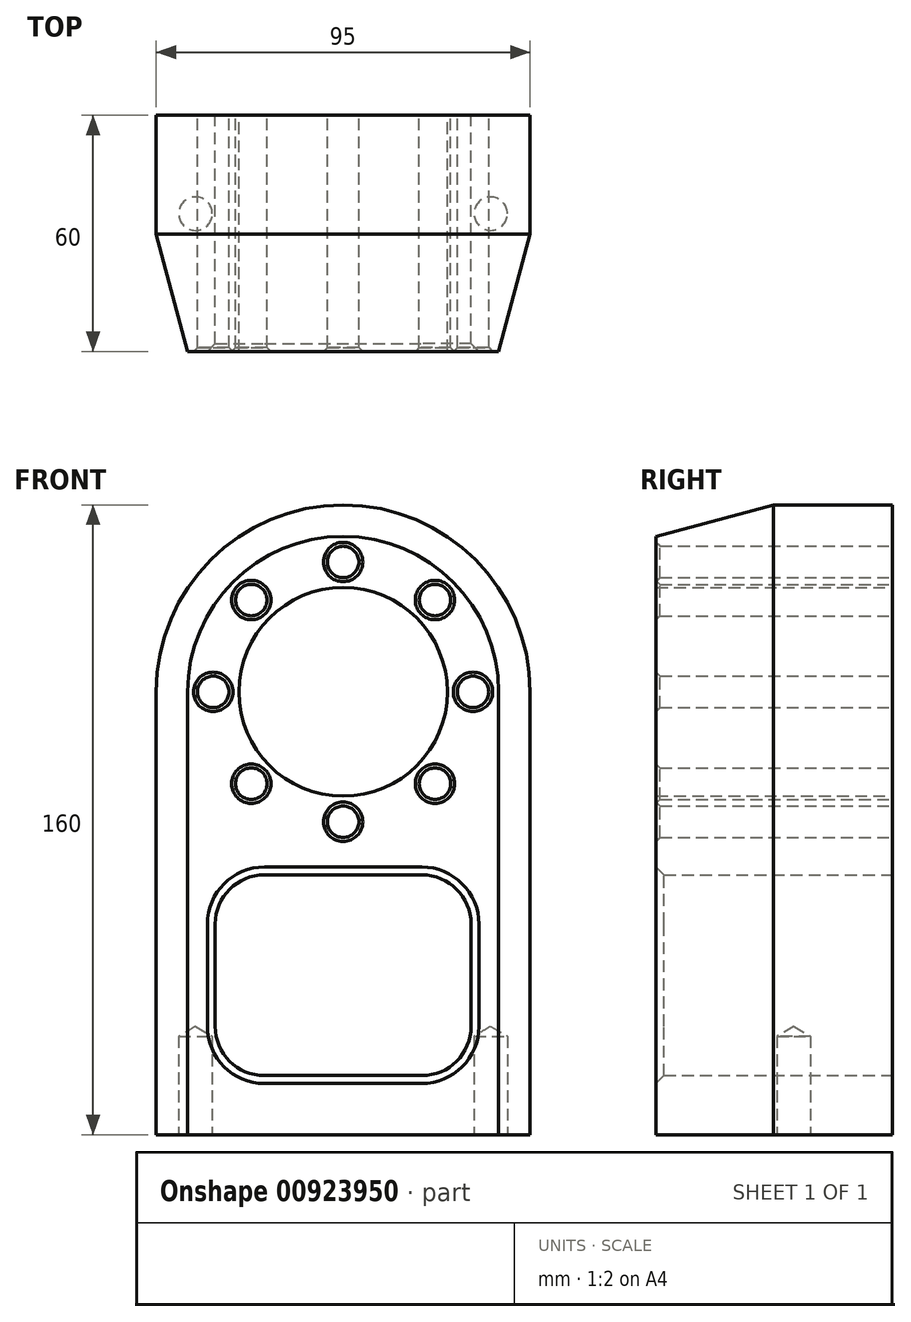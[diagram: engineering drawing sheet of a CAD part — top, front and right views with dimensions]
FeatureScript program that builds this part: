
annotation { "Feature Type Name" : "Feature", "Feature Type Description" : "" }
export const myFeature = defineFeature(function(context is Context, id is Id, definition is map)
    precondition{}
    {
        {
            var Q0;
            Q0=qCreatedBy(makeId("Front.planeOp"),FACE);
            var sketch = newSketch(context, id + "F0", { "sketchPlane" : qUnion([Q0])});
            skLineSegment(sketch, "E0.top", {"start": v(-46, -58.24) * mm, "end": v(49, -58.24) * mm});
            skLineSegment(sketch, "E0.left", {"start": v(-46, 54.26) * mm, "end": v(-46, -58.24) * mm});
            skLineSegment(sketch, "E0.right", {"start": v(49, 54.26) * mm, "end": v(49, -58.24) * mm});
            skArc(sketch, "E1", {"start": v(49, 54.26) * mm, "mid": v(1.5, 101.76) * mm, "end": v(-46, 54.26) * mm});
            skCircle(sketch, "E2", {"center": v(1.5, 54.26) * mm, "radius": 26.5 * mm});
            skLineSegment(sketch, "E3.bottom", {"start": v(-18.5, 7.76) * mm, "end": v(21.5, 7.76) * mm});
            skLineSegment(sketch, "E3.top", {"start": v(-18.5, -43.24) * mm, "end": v(21.5, -43.24) * mm});
            skLineSegment(sketch, "E3.left", {"start": v(-31, -4.74) * mm, "end": v(-31, -30.74) * mm});
            skLineSegment(sketch, "E3.right", {"start": v(34, -4.74) * mm, "end": v(34, -30.74) * mm});
            skPoint(sketch, "E4.visualSharp", {"position": v(-31, 7.76) * mm});
            skArc(sketch, "E4.filletArc", {"start": v(-18.5, 7.76) * mm, "mid": v(-27.34, 4.1) * mm, "end": v(-31, -4.74) * mm});
            skPoint(sketch, "E5.visualSharp", {"position": v(34, 7.76) * mm});
            skArc(sketch, "E5.filletArc", {"start": v(34, -4.74) * mm, "mid": v(30.34, 4.1) * mm, "end": v(21.5, 7.76) * mm});
            skPoint(sketch, "E6.visualSharp", {"position": v(34, -43.24) * mm});
            skArc(sketch, "E6.filletArc", {"start": v(21.5, -43.24) * mm, "mid": v(30.34, -39.58) * mm, "end": v(34, -30.74) * mm});
            skPoint(sketch, "E7.visualSharp", {"position": v(-31, -43.24) * mm});
            skArc(sketch, "E7.filletArc", {"start": v(-31, -30.74) * mm, "mid": v(-27.34, -39.58) * mm, "end": v(-18.5, -43.24) * mm});
            skLineSegment(sketch, "E8", {"start": v(1.5, 54.26) * mm, "end": v(-66.33, 54.26) * mm, "construction": true});
            skCircle(sketch, "E9", {"center": v(-31.5, 54.26) * mm, "radius": 4 * mm});
            skCircle(sketch, "E10.1.0", {"center": v(-21.83, 77.6) * mm, "radius": 4 * mm});
            skCircle(sketch, "E10.2.0", {"center": v(1.5, 87.26) * mm, "radius": 4 * mm});
            skCircle(sketch, "E10.3.0", {"center": v(24.84, 77.6) * mm, "radius": 4 * mm});
            skCircle(sketch, "E10.4.0", {"center": v(34.5, 54.26) * mm, "radius": 4 * mm});
            skCircle(sketch, "E10.5.0", {"center": v(24.84, 30.93) * mm, "radius": 4 * mm});
            skCircle(sketch, "E10.6.0", {"center": v(1.5, 21.26) * mm, "radius": 4 * mm});
            skCircle(sketch, "E10.7.0", {"center": v(-21.83, 30.93) * mm, "radius": 4 * mm});
            skSolve(sketch);
        }
        {
            var Q0;
            Q0 = qSketchRegion(id + "F0", true);
            extrude(context, id + "F1", {"entities" : qUnion([Q0]), "depth" : 60 * mm, "offsetDistance" : 25 * mm});
        }
        {
            var Q0;
            Q0=makeQuery(id+"F1.opExtrude","CAP_EDGE",EDGE,{"disambiguationData":[OSD([sQuery(id+"F0.wireOp",EDGE,"E9")])],"isStart":false});
            var Q1;
            Q1=makeQuery(id+"F1.opExtrude","CAP_EDGE",EDGE,{"disambiguationData":[OSD([sQuery(id+"F0.wireOp",EDGE,"E10.1.0")])],"isStart":false});
            var Q2;
            Q2=makeQuery(id+"F1.opExtrude","CAP_EDGE",EDGE,{"disambiguationData":[OSD([sQuery(id+"F0.wireOp",EDGE,"E10.2.0")])],"isStart":false});
            var Q3;
            Q3=makeQuery(id+"F1.opExtrude","CAP_EDGE",EDGE,{"disambiguationData":[OSD([sQuery(id+"F0.wireOp",EDGE,"E10.3.0")])],"isStart":false});
            var Q4;
            Q4=makeQuery(id+"F1.opExtrude","CAP_EDGE",EDGE,{"disambiguationData":[OSD([sQuery(id+"F0.wireOp",EDGE,"E10.4.0")])],"isStart":false});
            var Q5;
            Q5=makeQuery(id+"F1.opExtrude","CAP_EDGE",EDGE,{"disambiguationData":[OSD([sQuery(id+"F0.wireOp",EDGE,"E10.5.0")])],"isStart":false});
            var Q6;
            Q6=makeQuery(id+"F1.opExtrude","CAP_EDGE",EDGE,{"disambiguationData":[OSD([sQuery(id+"F0.wireOp",EDGE,"E10.6.0")])],"isStart":false});
            var Q7;
            Q7=makeQuery(id+"F1.opExtrude","CAP_EDGE",EDGE,{"disambiguationData":[OSD([sQuery(id+"F0.wireOp",EDGE,"E10.7.0")])],"isStart":false});
            chamfer(context, id + "F2", {"entities" : qUnion([Q0, Q1, Q2, Q3, Q4, Q5, Q6, Q7]), "width" : 1 * mm, "tangentPropagation" : true});
        }
        {
            var Q0;
            Q0=makeQuery(id+"F1.opExtrude","CAP_EDGE",EDGE,{"disambiguationData":[OSD([sQuery(id+"F0.wireOp",EDGE,"E3.bottom")])],"isStart":false});
            chamfer(context, id + "F3", {"entities" : qUnion([Q0]), "width" : 2 * mm, "tangentPropagation" : true});
        }
        {
            var Q0;
            Q0=makeQuery(id+"F1.opExtrude","CAP_EDGE",EDGE,{"disambiguationData":[OSD([sQuery(id+"F0.wireOp",EDGE,"E1")])],"isStart":false});
            chamfer(context, id + "F4", {"entities" : qUnion([Q0]), "chamferType" : ChamferType.OFFSET_ANGLE, "width" : 8 * mm, "oppositeDirection" : false, "angle" : 75 * degree, "tangentPropagation" : true});
        }
        {
            var Q0;
            Q0=makeQuery(id+"F1.opExtrude","SWEPT_FACE",FACE,{"disambiguationData":[OSD([sQuery(id+"F0.wireOp",EDGE,"E0.top")])]});
            var sketch = newSketch(context, id + "F5", { "sketchPlane" : qUnion([Q0])});
            skLineSegment(sketch, "E11", {"start": v(-96.32, 25) * mm, "end": v(117.52, 25) * mm, "construction": true});
            skPoint(sketch, "E12", {"position": v(-36, 25) * mm});
            skPoint(sketch, "E13", {"position": v(39, 25) * mm});
            skSolve(sketch);
        }
        {
            var Q0;
            Q0=sQuery(id+"F5.wireOp",VERTEX,"E12");
            var Q1;
            Q1=sQuery(id+"F5.wireOp",VERTEX,"E13");
            var Q2;
            Q2=makeQuery(id+"F1.opExtrude","SWEPT_BODY",BODY,{"disambiguationData":[OSD([sQuery(id+"F0.wireOp",EDGE,"E0.top"),sQuery(id+"F0.wireOp",EDGE,"E0.left"),sQuery(id+"F0.wireOp",EDGE,"E0.right"),sQuery(id+"F0.wireOp",EDGE,"E1"),sQuery(id+"F0.wireOp",EDGE,"E2"),sQuery(id+"F0.wireOp",EDGE,"E3.bottom"),sQuery(id+"F0.wireOp",EDGE,"E3.top"),sQuery(id+"F0.wireOp",EDGE,"E3.left"),sQuery(id+"F0.wireOp",EDGE,"E3.right"),sQuery(id+"F0.wireOp",EDGE,"E4.filletArc"),sQuery(id+"F0.wireOp",EDGE,"E5.filletArc"),sQuery(id+"F0.wireOp",EDGE,"E6.filletArc"),sQuery(id+"F0.wireOp",EDGE,"E7.filletArc"),sQuery(id+"F0.wireOp",EDGE,"E9"),sQuery(id+"F0.wireOp",EDGE,"E10.1.0"),sQuery(id+"F0.wireOp",EDGE,"E10.2.0"),sQuery(id+"F0.wireOp",EDGE,"E10.3.0"),sQuery(id+"F0.wireOp",EDGE,"E10.4.0"),sQuery(id+"F0.wireOp",EDGE,"E10.5.0"),sQuery(id+"F0.wireOp",EDGE,"E10.6.0"),sQuery(id+"F0.wireOp",EDGE,"E10.7.0")])]});
            hole(context, id + "F6", {"style" : HoleStyle.SIMPLE, "endStyle" : HoleEndStyle.BLIND, "standardTappedOrClearance" : lookupTablePath({ "standard" : "ISO", "engagement" : "75%", "pitch" : "1.5 mm", "size" : "M10", "type" : "Tapped" }), "standardBlindInLast" : lookupTablePath({ "standard" : "ISO", "engagement" : "75%", "pitch" : "1.5 mm", "size" : "M10", "type" : "Tapped" }), "holeDiameter" : 8.5 * mm, "majorDiameter" : 10 * mm, "showTappedDepth" : true, "holeDepth" : 25 * mm, "isTappedThrough" : true, "tappedDepth" : 20.5 * mm, "tapClearance" : 3, "locations" : qUnion([Q0, Q1]), "scope" : qUnion([Q2])});
        }
    });
